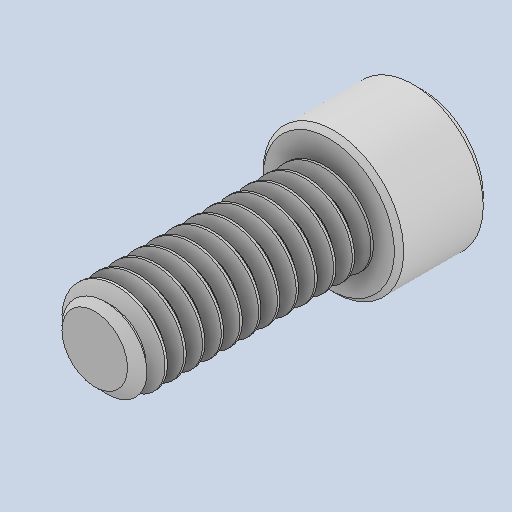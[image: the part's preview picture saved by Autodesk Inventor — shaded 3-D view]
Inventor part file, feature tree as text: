
AUTODESK INVENTOR PART (.ipt)
format: ipt  version: 2022.3 (Build 263350000, 350)  size: 570,368 bytes
history: native  units: in
note: dims shown in document units (in); Inventor stores cm internally (conversion verified against a paired STEP export)
features: chamfer x1
ambient origin geometry x8: Origin, YZ Plane, XZ Plane, XY Plane, X Axis, Y Axis, Z Axis, Center Point
bodies: Solid1 (feature_tree)
feature tree (1):
  chamfer  "Chamfer2"  [1 undecoded]
note: 1 required parameter value undecoded (feature->parameter linkage not recoverable at this tier; creation-order binding heuristic only, values carry confidence <= 0.55)
